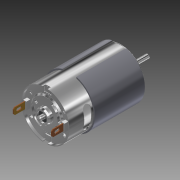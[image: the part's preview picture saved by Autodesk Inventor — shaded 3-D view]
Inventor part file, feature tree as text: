
AUTODESK INVENTOR PART (.ipt)
format: ipt  version: 2016 SP1 (Build 200210100, 210)  size: 926,208 bytes
history: native  units: mm (DEFAULTED — no unit token found)
features: extrude x24, sketch x24, fillet x7, plane x6, mirror x4, projected_geometry x3, chamfer x2, pattern_circular x2, shell x1, revolve x1
ambient origin geometry x8: Origin, YZ Plane, XZ Plane, XY Plane, X Axis, Y Axis, Z Axis, Center Point
bodies: Solid1 (feature_tree)
feature tree (74):
  extrude  "Extrusion1"  Depth=56.896mm TaperAngle=0.0deg
  fillet  "Fillet1"  Radius=2.0mm
  shell  "Shell1"  Thickness=0.62mm
  extrude  "Extrusion2"  Depth=4.572mm TaperAngle=0.0deg
  fillet  "Fillet2"  Radius=0.5mm
  plane  "Work Plane1"
  extrude  "Extrusion5"  Depth=0.62mm TaperAngle=0.0deg
  extrude  "Extrusion6"  Depth=1.016mm
  fillet  "Fillet4"  Radius=0.6096mm
  fillet  "Fillet5"  Radius=4.9276mm
  extrude  "Extrusion11"  Depth=11.43mm TaperAngle=0.0deg
  chamfer  "Chamfer1"  Distance=1.0mm
  sketch  "Sketch13"  dims[d61=3.0mm d69=18.0mm]
  mirror  "Mirror2"
  plane  "Work Plane2"
  plane  "Work Plane3"
  extrude  "Flux Ring"  Depth=18.0mm
  extrude  "Extrusion15"  Depth=1.016mm
  mirror  "Mirror3"
  sketch  "Sketch18"  dims[d83=0.254mm d93=2.413mm]
  extrude  "Extrusion16"  Depth=0.254mm
  extrude  "Extrusion17"  Depth=2.413mm
  chamfer  "Chamfer2"  Distance=2.921mm
  extrude  "Extrusion18"  Depth=3.429mm TaperAngle=0.0deg
  extrude  "Extrusion19"  Depth=3.429mm TaperAngle=0.0deg
  extrude  "Extrusion20"  Depth=1.397mm TaperAngle=0.0deg
  fillet  "Fillet9"  Radius=3.175mm
  extrude  "Extrusion21"  Depth=1.016mm
  extrude  "Extrusion22"  Depth=3.8862mm TaperAngle=0.0deg
  extrude  "Extrusion24"  Depth=0.508mm
  extrude  "Extrusion25"  Depth=1.016mm
  extrude  "Extrusion26"  Depth=3.8862mm TaperAngle=0.0deg
  plane  "Work Plane4"
  extrude  "Extrusion29"  Depth=1.860192mm
  fillet  "Fillet10"  Radius=3.699166mm
  extrude  "Extrusion30"  Depth=0.381mm
  fillet  "Fillet11"  Radius=0.6096mm
  mirror  "Mirror4"
  extrude  "Extrusion31"  Depth=1.27mm TaperAngle=0.0deg
  sketch  "Sketch29"  dims[d153=1.27mm d154=0.0mm d155=0.381mm d156=0.6096mm d157=0.0mm]
  extrude  "Extrusion32"  Depth=0.785398mm
  pattern_circular  "Circular Pattern4"  Count=40 Angle=360.0deg
  extrude  "Extrusion34"  Depth=2.949849mm
  pattern_circular  "Circular Pattern5"  [2 undecoded]
  revolve  "Revolution1"  [1 undecoded]
  extrude  "Extrusion35"  Depth=10.0076mm TaperAngle=0.0deg
  plane  "Work Plane6"
  extrude  "Extrusion36"  Depth=400.0mm TaperAngle=360.0deg
  mirror  "Mirror5"
  sketch  "Sketch1"  dims[d0=35.7886mm d1=56.896mm d2=0.0mm d3=2.0mm d4=0.62mm]
  sketch  "Sketch2"  dims[d5=13.0mm d6=4.572mm d7=0.0mm d8=0.5mm]
  sketch  "Sketch6"  dims[d30=-1.905mm d31=0.62mm d32=0.0mm]
  sketch  "Sketch7"  dims[d33=24.13mm d34=1.016mm d35=-7.853982mm d54=0.6096mm d55=4.9276mm]
  sketch  "Sketch12"  dims[d56=13.843mm d57=11.43mm d58=0.0mm d59=1.0mm d60=2.0mm]
  sketch  "Sketch15"  dims[d75=45.0deg d76=1.016mm]
  sketch  "Sketch17"  dims[d77=36.8808mm d78=0.0mm d82=0.254mm]
  sketch  "Sketch19"  dims[d95=5.588mm d96=2.921mm d97=0.0mm]
  sketch  "Sketch20"  dims[d102=25.4mm d103=0.0mm d104=3.429mm d105=0.0mm]
  sketch  "Sketch21"  dims[d106=0.508mm d107=1.27mm d108=45.0deg d109=3.429mm d110=0.0mm]
  sketch  "Sketch22"  dims[d111=3.6576mm d114=1.397mm d115=0.0mm d116=3.175mm]
  sketch  "Sketch23"  dims[d117=3.8862mm d118=77.0128mm d119=0.0mm d120=0.0mm d121=1.016mm]
  sketch  "Sketch24"  dims[d123=3.8862mm d124=0.0mm d125=3.8862mm d126=0.0mm]
  sketch  "Sketch25"  dims[d129=3.8862mm d130=0.0mm d137=0.508mm]
  projected_geometry  "Projected Loop1"
  sketch  "Sketch26"  dims[d139=0.508mm d140=1.016mm]
  projected_geometry  "Projected Loop2"
  sketch  "Sketch27"  dims[d141=0.508mm d142=3.8862mm d143=0.0mm]
  plane  "Work Plane5"
  sketch  "Sketch28"  dims[d144=0.6096mm d145=0.0mm d150=1.860192mm d152=3.699166mm]
  sketch  "Sketch30"  dims[d158=0.381mm d159=1.27mm d160=0.0mm]
  sketch  "Sketch31"  dims[d162=1.570796mm d163=0.785398mm]
  projected_geometry  "Projected Loop3"
  sketch  "Sketch32"  dims[d165=10.0076mm d166=0.0mm d167=400.0mm d168=360.0deg]
  sketch  "Sketch33"  dims[d170=3.200082mm d172=2.949849mm d173=1.570796mm d174=14.57284mm d178=10.0076mm d179=0.0mm d180=400.0mm d181=360.0deg d186=45.0deg d187=90.0deg d188=0.127mm d189=5.08mm d190=5.08mm d191=10.0076mm d192=0.0mm d193=1.27mm d194=5.715mm d195=10.668mm d196=5.334mm d197=10.0076mm d198=0.0mm]
note: 3 required parameter values undecoded (feature->parameter linkage not recoverable at this tier; creation-order binding heuristic only, values carry confidence <= 0.55)